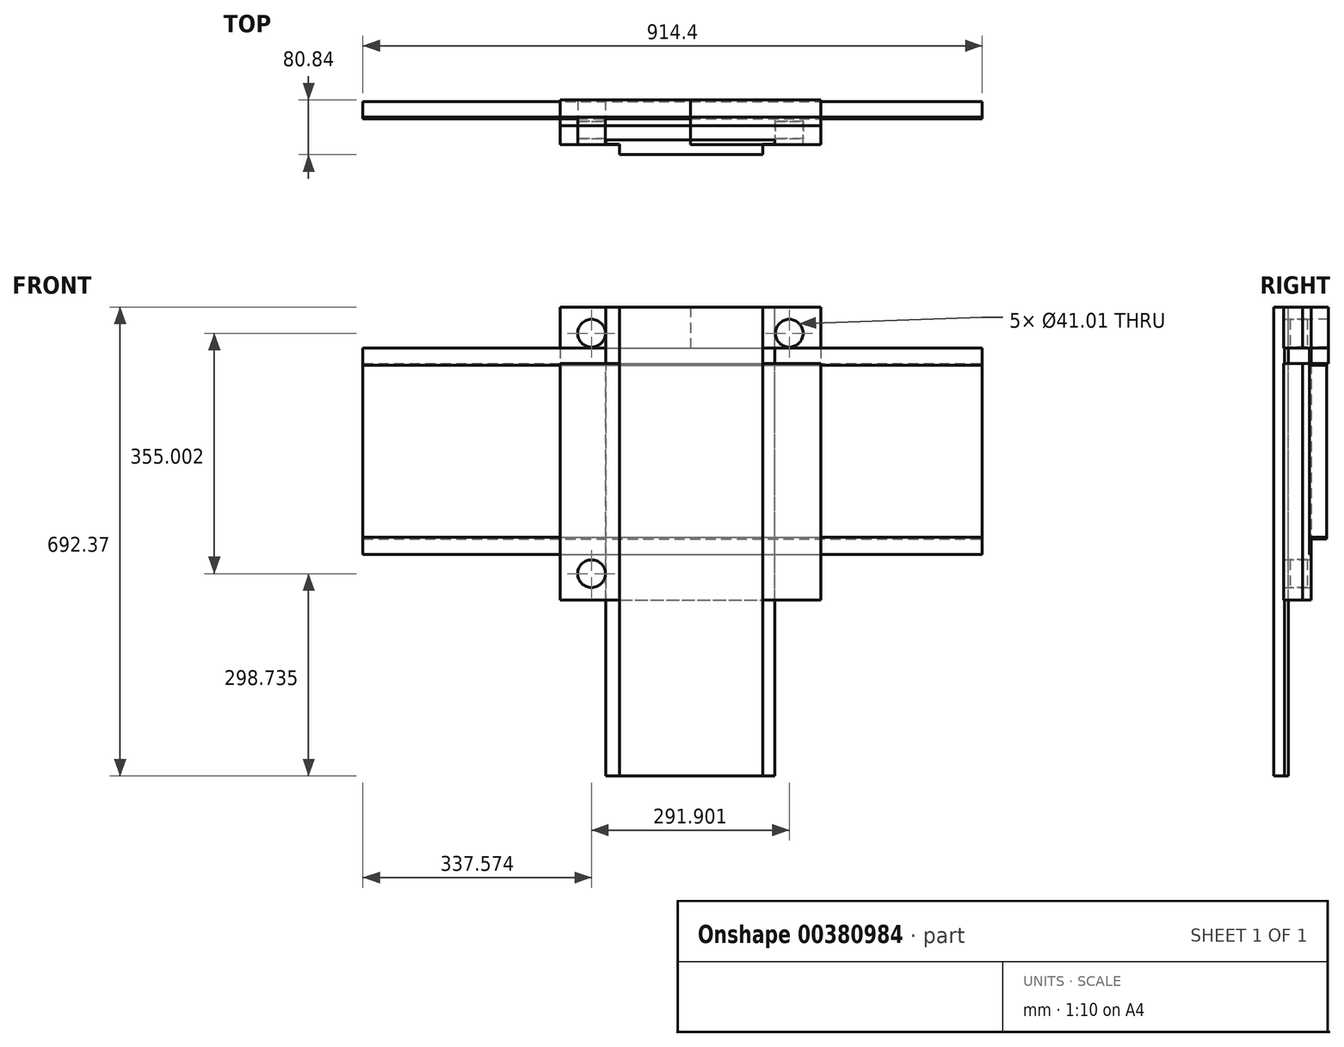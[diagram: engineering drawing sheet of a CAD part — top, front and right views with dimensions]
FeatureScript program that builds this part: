
annotation { "Feature Type Name" : "Feature", "Feature Type Description" : "" }
export const myFeature = defineFeature(function(context is Context, id is Id, definition is map)
    precondition{}
    {
        {
            var Q0;
            Q0=qCreatedBy(makeId("Front.planeOp"),FACE);
            var sketch = newSketch(context, id + "F0", { "sketchPlane" : qUnion([Q0])});
            skLineSegment(sketch, "E0.bottom", {"start": v(-127.83, -64.5) * mm, "end": v(786.57, -64.5) * mm});
            skLineSegment(sketch, "E0.top", {"start": v(-127.83, 189.5) * mm, "end": v(786.57, 189.5) * mm});
            skLineSegment(sketch, "E0.left", {"start": v(-127.83, -64.5) * mm, "end": v(-127.83, 189.5) * mm});
            skLineSegment(sketch, "E0.right", {"start": v(786.57, -64.5) * mm, "end": v(786.57, 189.5) * mm});
            skSolve(sketch);
        }
        {
            var Q0;
            Q0=makeQuery(id+"F0.imprint","IMPRINT",FACE,{"disambiguationData":[TD([[makeQuery(id+"F0.imprint","IMPRINT",EDGE,{"derivedFrom":sQuery(id+"F0.wireOp",EDGE,"E0.bottom")}),1.0]])]});
            extrude(context, id + "F1", {"entities" : qUnion([Q0]), "depth" : 25.4 * mm});
        }
        {
            var Q0;
            Q0=makeQuery(id+"F1.opExtrude","SWEPT_FACE",FACE,{"disambiguationData":[OSD([sQuery(id+"F0.wireOp",EDGE,"E0.right")])]});
            var sketch = newSketch(context, id + "F2", { "sketchPlane" : qUnion([Q0])});
            skLineSegment(sketch, "E1.bottom", {"start": v(-25.4, 189.5) * mm, "end": v(0, 189.5) * mm});
            skLineSegment(sketch, "E1.top", {"start": v(-25.4, 192.27) * mm, "end": v(0, 192.27) * mm});
            skLineSegment(sketch, "E1.left", {"start": v(-25.4, 189.5) * mm, "end": v(-25.4, 192.27) * mm});
            skLineSegment(sketch, "E1.right", {"start": v(0, 189.5) * mm, "end": v(0, 192.27) * mm});
            skLineSegment(sketch, "E2.bottom", {"start": v(-25.4, 189.5) * mm, "end": v(-22.75, 189.5) * mm});
            skLineSegment(sketch, "E2.top", {"start": v(-25.4, 214.9) * mm, "end": v(-22.75, 214.9) * mm});
            skLineSegment(sketch, "E2.left", {"start": v(-25.4, 189.5) * mm, "end": v(-25.4, 214.9) * mm});
            skLineSegment(sketch, "E2.right", {"start": v(-22.75, 189.5) * mm, "end": v(-22.75, 214.9) * mm});
            skSolve(sketch);
        }
        {
            var Q0;
            {var subQ0=sQuery(id+"F2.wireOp",EDGE,"E1.bottom");Q0=makeQuery(id+"F2.imprint","IMPRINT",FACE,{"disambiguationData":[TD([[makeQuery(id+"F2.imprint","IMPRINT",EDGE,{"derivedFrom":subQ0}),1.0]])]});}
            var Q1;
            {var subQ5=sQuery(id+"F2.wireOp",EDGE,"E2.bottom");Q1=makeQuery(id+"F2.imprint","IMPRINT",FACE,{"disambiguationData":[TD([[makeQuery(id+"F2.imprint","IMPRINT",EDGE,{"derivedFrom":subQ5}),1.0]])]});}
            var Q2;
            {var subQ5=sQuery(id+"F2.wireOp",EDGE,"E2.top");Q2=makeQuery(id+"F2.imprint","IMPRINT",FACE,{"disambiguationData":[TD([[makeQuery(id+"F2.imprint","IMPRINT",EDGE,{"derivedFrom":subQ5}),-1.0]])]});}
            extrude(context, id + "F3", {"entities" : qUnion([Q0, Q1, Q2]), "oppositeDirection" : true, "depth" : 914.4 * mm});
        }
        {
            var Q0;
            Q0=makeQuery(id+"F3.opExtrude","SWEPT_BODY",BODY,{"disambiguationData":[OSD([sQuery(id+"F2.wireOp",EDGE,"E1.bottom"),sQuery(id+"F2.wireOp",EDGE,"E1.top"),sQuery(id+"F2.wireOp",EDGE,"E1.right"),sQuery(id+"F2.wireOp",EDGE,"E2.bottom"),sQuery(id+"F2.wireOp",EDGE,"E2.top"),sQuery(id+"F2.wireOp",EDGE,"E2.left"),sQuery(id+"F2.wireOp",EDGE,"E2.right")])]});
            var Q1;
            Q1=makeQuery(id+"F1.opExtrude","SWEPT_FACE",FACE,{"disambiguationData":[OSD([sQuery(id+"F0.wireOp",EDGE,"E0.bottom")])]});
            mirror(context, id + "F4", {"entities" : qUnion([Q0]), "mirrorPlane" : qUnion([Q1])});
        }
        {
            var Q0;
            Q0=makeQuery(id+"F4.opPattern","COPY",BODY,{"derivedFrom":makeQuery(id+"F3.opExtrude","SWEPT_BODY",BODY,{"disambiguationData":[OSD([sQuery(id+"F2.wireOp",EDGE,"E1.bottom"),sQuery(id+"F2.wireOp",EDGE,"E1.top"),sQuery(id+"F2.wireOp",EDGE,"E1.right"),sQuery(id+"F2.wireOp",EDGE,"E2.bottom"),sQuery(id+"F2.wireOp",EDGE,"E2.top"),sQuery(id+"F2.wireOp",EDGE,"E2.left"),sQuery(id+"F2.wireOp",EDGE,"E2.right")])]}),"instanceName":"1"});
            transform(context, id + "F5", {"entities" : qUnion([Q0]), "transformType" : TransformType.TRANSLATION_3D, "dx" : 0 * mm, "dy" : 0 * mm, "dz" : 254.36 * mm, "makeCopy" : false});
        }
        {
            var Q0;
            Q0=makeQuery(id+"F3.opExtrude","SWEPT_FACE",FACE,{"disambiguationData":[OSD([sQuery(id+"F2.wireOp",EDGE,"E2.right")])]});
            var sketch = newSketch(context, id + "F6", { "sketchPlane" : qUnion([Q0])});
            skCircle(sketch, "E3", {"center": v(-209.74, 236.98) * mm, "radius": 20.5 * mm});
            skLineSegment(sketch, "E4.bottom", {"start": v(-163.24, 275.6) * mm, "end": v(-548.15, 275.6) * mm});
            skLineSegment(sketch, "E4.top", {"start": v(-163.24, -156.66) * mm, "end": v(-548.15, -156.66) * mm});
            skLineSegment(sketch, "E4.left", {"start": v(-163.24, 275.6) * mm, "end": v(-163.24, -156.66) * mm});
            skLineSegment(sketch, "E4.right", {"start": v(-548.15, 275.6) * mm, "end": v(-548.15, -156.66) * mm});
            skLineSegment(sketch, "E5", {"start": v(-355.7, 275.6) * mm, "end": v(-355.7, 159.7) * mm});
            skCircle(sketch, "E6.MirrorC", {"center": v(-501.64, 236.98) * mm, "radius": 20.5 * mm});
            skLineSegment(sketch, "E7", {"start": v(-163.24, 59.48) * mm, "end": v(-279.66, 59.48) * mm});
            skLineSegment(sketch, "E8", {"start": v(-355.7, -156.66) * mm, "end": v(-355.7, -17.47) * mm});
            skCircle(sketch, "E9.MirrorC", {"center": v(-209.74, -118.03) * mm, "radius": 20.5 * mm});
            skCircle(sketch, "E10.MirrorC", {"center": v(-501.64, -118.03) * mm, "radius": 20.5 * mm});
            skSolve(sketch);
        }
        {
            var Q0;
            Q0=makeQuery(id+"F6.imprint","IMPRINT",FACE,{"disambiguationData":[TD([[makeQuery(id+"F6.imprint","IMPRINT",EDGE,{"derivedFrom":sQuery(id+"F6.wireOp",EDGE,"E9.MirrorC")}),-1.0]])]});
            var Q1;
            Q1=makeQuery(id+"F6.imprint","IMPRINT",FACE,{"disambiguationData":[TD([[makeQuery(id+"F6.imprint","IMPRINT",EDGE,{"derivedFrom":sQuery(id+"F6.wireOp",EDGE,"E10.MirrorC")}),1.0]])]});
            var Q2;
            Q2=makeQuery(id+"F6.imprint","IMPRINT",FACE,{"disambiguationData":[TD([[makeQuery(id+"F6.imprint","IMPRINT",EDGE,{"derivedFrom":sQuery(id+"F6.wireOp",EDGE,"E6.MirrorC")}),-1.0]])]});
            var Q3;
            Q3=makeQuery(id+"F6.imprint","IMPRINT",FACE,{"disambiguationData":[TD([[makeQuery(id+"F6.imprint","IMPRINT",EDGE,{"derivedFrom":sQuery(id+"F6.wireOp",EDGE,"E3")}),1.0]])]});
            extrude(context, id + "F7", {"entities" : qUnion([Q0, Q1, Q2, Q3]), "oppositeDirection" : true, "depth" : 12.7 * mm});
        }
        {
            var Q0;
            Q0=makeQuery(id+"F6.imprint","IMPRINT",FACE,{"disambiguationData":[TD([[makeQuery(id+"F6.imprint","IMPRINT",EDGE,{"derivedFrom":sQuery(id+"F6.wireOp",EDGE,"E9.MirrorC")}),1.0]])]});
            var Q1;
            Q1=makeQuery(id+"F6.imprint","IMPRINT",FACE,{"disambiguationData":[TD([[makeQuery(id+"F6.imprint","IMPRINT",EDGE,{"derivedFrom":sQuery(id+"F6.wireOp",EDGE,"E6.MirrorC")}),1.0]])]});
            var Q2;
            Q2=makeQuery(id+"F6.imprint","IMPRINT",FACE,{"disambiguationData":[TD([[makeQuery(id+"F6.imprint","IMPRINT",EDGE,{"derivedFrom":sQuery(id+"F6.wireOp",EDGE,"E3")}),-1.0]])]});
            var Q3;
            {var subQ0=sQuery(id+"F6.wireOp",EDGE,"E4.right");var subQ1=sQuery(id+"F2.wireOp",EDGE,"E2.right");var subQ2=makeQuery(id+"F3.opExtrude","SWEPT_EDGE",EDGE,{"disambiguationData":[OSD([sQuery(id+"F2.wireOp",EDGE,"E2.top"),subQ1])]});var subQ3=makeQuery(id+"F6.imprint","INTERSECT",VERTEX,{"derivedFrom":[subQ2,subQ0]});Q3=makeQuery(id+"F6.imprint","IMPRINT",FACE,{"disambiguationData":[TD([[makeQuery(id+"F6.imprint","IMPRINT",EDGE,{"disambiguationData":[TD([[subQ3,-1.0]])],"derivedFrom":subQ0}),1.0]])]});}
            var Q4;
            {var subQ0=sQuery(id+"F6.wireOp",EDGE,"E4.left");var subQ1=sQuery(id+"F2.wireOp",EDGE,"E2.right");var subQ2=makeQuery(id+"F3.opExtrude","SWEPT_EDGE",EDGE,{"disambiguationData":[OSD([sQuery(id+"F2.wireOp",EDGE,"E2.top"),subQ1])]});var subQ3=makeQuery(id+"F6.imprint","INTERSECT",VERTEX,{"derivedFrom":[subQ2,subQ0]});Q4=makeQuery(id+"F6.imprint","IMPRINT",FACE,{"disambiguationData":[TD([[makeQuery(id+"F6.imprint","IMPRINT",EDGE,{"disambiguationData":[TD([[subQ3,-1.0]])],"derivedFrom":subQ0}),-1.0]])]});}
            extrude(context, id + "F8", {"entities" : qUnion([Q0, Q1, Q2, Q3, Q4]), "depth" : 25.4 * mm});
        }
        {
            var Q0;
            Q0=makeQuery(id+"F8.opExtrude","SWEPT_BODY",BODY,{"disambiguationData":[OSD([sQuery(id+"F6.wireOp",EDGE,"E3"),sQuery(id+"F6.wireOp",EDGE,"E4.bottom"),sQuery(id+"F6.wireOp",EDGE,"E4.top"),sQuery(id+"F6.wireOp",EDGE,"E4.left"),sQuery(id+"F6.wireOp",EDGE,"E4.right"),sQuery(id+"F6.wireOp",EDGE,"E6.MirrorC"),sQuery(id+"F6.wireOp",EDGE,"E9.MirrorC"),sQuery(id+"F6.wireOp",EDGE,"E10.MirrorC")])]});
            transform(context, id + "F9", {"entities" : qUnion([Q0]), "transformType" : TransformType.TRANSLATION_3D, "dx" : 0 * mm, "dy" : -31.35 * mm, "dz" : 0 * mm, "makeCopy" : false});
        }
        {
            var Q0;
            Q0=makeQuery(id+"F7.opExtrude","CAP_FACE",FACE,{"disambiguationData":[OSD([sQuery(id+"F6.wireOp",EDGE,"E6.MirrorC")])],"isStart":false});
            var Q1;
            Q1=makeQuery(id+"F7.opExtrude","CAP_FACE",FACE,{"disambiguationData":[OSD([sQuery(id+"F6.wireOp",EDGE,"E3")])],"isStart":false});
            var Q2;
            Q2=makeQuery(id+"F7.opExtrude","CAP_FACE",FACE,{"disambiguationData":[OSD([sQuery(id+"F6.wireOp",EDGE,"E9.MirrorC")])],"isStart":false});
            var Q3;
            Q3=makeQuery(id+"F7.opExtrude","CAP_FACE",FACE,{"disambiguationData":[OSD([sQuery(id+"F6.wireOp",EDGE,"E10.MirrorC")])],"isStart":false});
            extrude(context, id + "F10", {"entities" : qUnion([Q0, Q1, Q2, Q3]), "depth" : 28.04 * mm});
        }
        {
            var Q0;
            Q0=makeQuery(id+"F8.opExtrude","SWEPT_FACE",FACE,{"disambiguationData":[OSD([sQuery(id+"F6.wireOp",EDGE,"E4.bottom")])]});
            var sketch = newSketch(context, id + "F11", { "sketchPlane" : qUnion([Q0])});
            skLineSegment(sketch, "E11", {"start": v(230.98, -62.48) * mm, "end": v(251.01, -62.48) * mm});
            skLineSegment(sketch, "E12", {"start": v(251.01, -62.48) * mm, "end": v(251.01, -78.2) * mm});
            skLineSegment(sketch, "E13", {"start": v(251.01, -78.2) * mm, "end": v(462.4, -78.2) * mm});
            skLineSegment(sketch, "E14", {"start": v(462.4, -78.2) * mm, "end": v(462.4, -62.46) * mm});
            skLineSegment(sketch, "E15", {"start": v(462.4, -62.46) * mm, "end": v(480.17, -62.46) * mm});
            skLineSegment(sketch, "E16", {"start": v(480.17, -62.46) * mm, "end": v(480.17, -56.45) * mm});
            skLineSegment(sketch, "E17", {"start": v(480.17, -56.45) * mm, "end": v(400.54, -56.45) * mm});
            skLineSegment(sketch, "E18", {"start": v(400.54, -56.45) * mm, "end": v(231.12, -56.45) * mm});
            skLineSegment(sketch, "E19", {"start": v(231.12, -56.45) * mm, "end": v(230.98, -62.48) * mm});
            skSolve(sketch);
        }
        {
            var Q0;
            Q0 = qSketchRegion(id + "F11", true);
            extrude(context, id + "F12", {"entities" : qUnion([Q0]), "oppositeDirection" : true, "depth" : 692.37 * mm});
        }
    });
